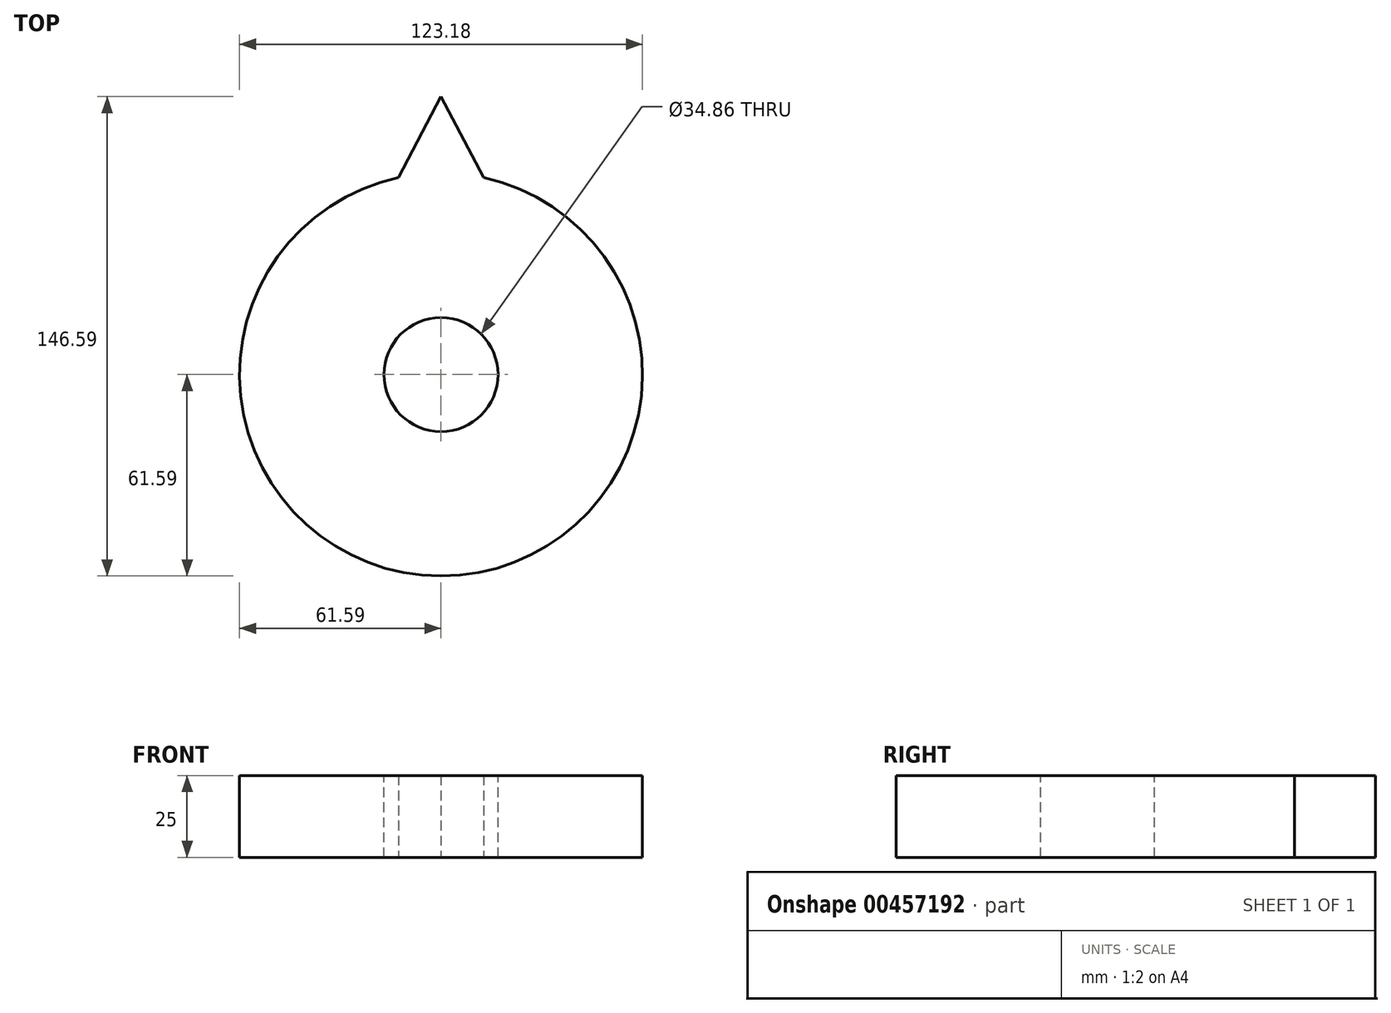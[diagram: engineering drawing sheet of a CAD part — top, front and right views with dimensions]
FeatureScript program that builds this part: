
annotation { "Feature Type Name" : "Feature", "Feature Type Description" : "" }
export const myFeature = defineFeature(function(context is Context, id is Id, definition is map)
    precondition{}
    {
        {
            var Q0;
            Q0=qCreatedBy(makeId("Top.planeOp"),FACE);
            var sketch = newSketch(context, id + "F0", { "sketchPlane" : qUnion([Q0])});
            skCircle(sketch, "E0", {"center": v(0, 0) * mm, "radius": 61.59 * mm});
            skSolve(sketch);
        }
        {
            var Q0;
            Q0=makeQuery(id+"F0.imprint","IMPRINT",FACE,{"disambiguationData":[TD([[makeQuery(id+"F0.imprint","IMPRINT",EDGE,{"derivedFrom":sQuery(id+"F0.wireOp",EDGE,"E0")}),1.0]])]});
            extrude(context, id + "F1", {"entities" : qUnion([Q0]), "depth" : 25 * mm});
        }
        {
            var Q0;
            Q0=makeQuery(id+"F1.opExtrude","CAP_FACE",FACE,{"disambiguationData":[OSD([sQuery(id+"F0.wireOp",EDGE,"E0")])],"isStart":false});
            var sketch = newSketch(context, id + "F2", { "sketchPlane" : qUnion([Q0])});
            skCircle(sketch, "E1", {"center": v(0, 0) * mm, "radius": 17.43 * mm});
            skSolve(sketch);
        }
        {
            var Q0;
            Q0 = qSketchRegion(id + "F2", true);
            extrude(context, id + "F3", {"entities" : qUnion([Q0]), "operationType" : NewBodyOperationType.REMOVE, "oppositeDirection" : true, "depth" : 25 * mm});
        }
        {
            var Q0;
            Q0=qCreatedBy(makeId("Top.planeOp"),FACE);
            var sketch = newSketch(context, id + "F4", { "sketchPlane" : qUnion([Q0])});
            skLineSegment(sketch, "E2", {"start": v(-13, 60.2) * mm, "end": v(0, 85) * mm});
            skLineSegment(sketch, "E3", {"start": v(0, 85) * mm, "end": v(13, 60.2) * mm});
            skArc(sketch, "E4.0", {"start": v(13, 60.2) * mm, "mid": v(0, 61.59) * mm, "end": v(-13, 60.2) * mm});
            skLineSegment(sketch, "E5", {"start": v(0, 0) * mm, "end": v(0, 85) * mm, "construction": true});
            skSolve(sketch);
        }
        {
            var Q0;
            Q0=makeQuery(id+"F4.imprint","IMPRINT",FACE,{"disambiguationData":[TD([[makeQuery(id+"F4.imprint","IMPRINT",EDGE,{"derivedFrom":sQuery(id+"F4.wireOp",EDGE,"E2")}),-1.0]])]});
            extrude(context, id + "F5", {"entities" : qUnion([Q0]), "operationType" : NewBodyOperationType.ADD, "depth" : 25 * mm});
        }
    });
